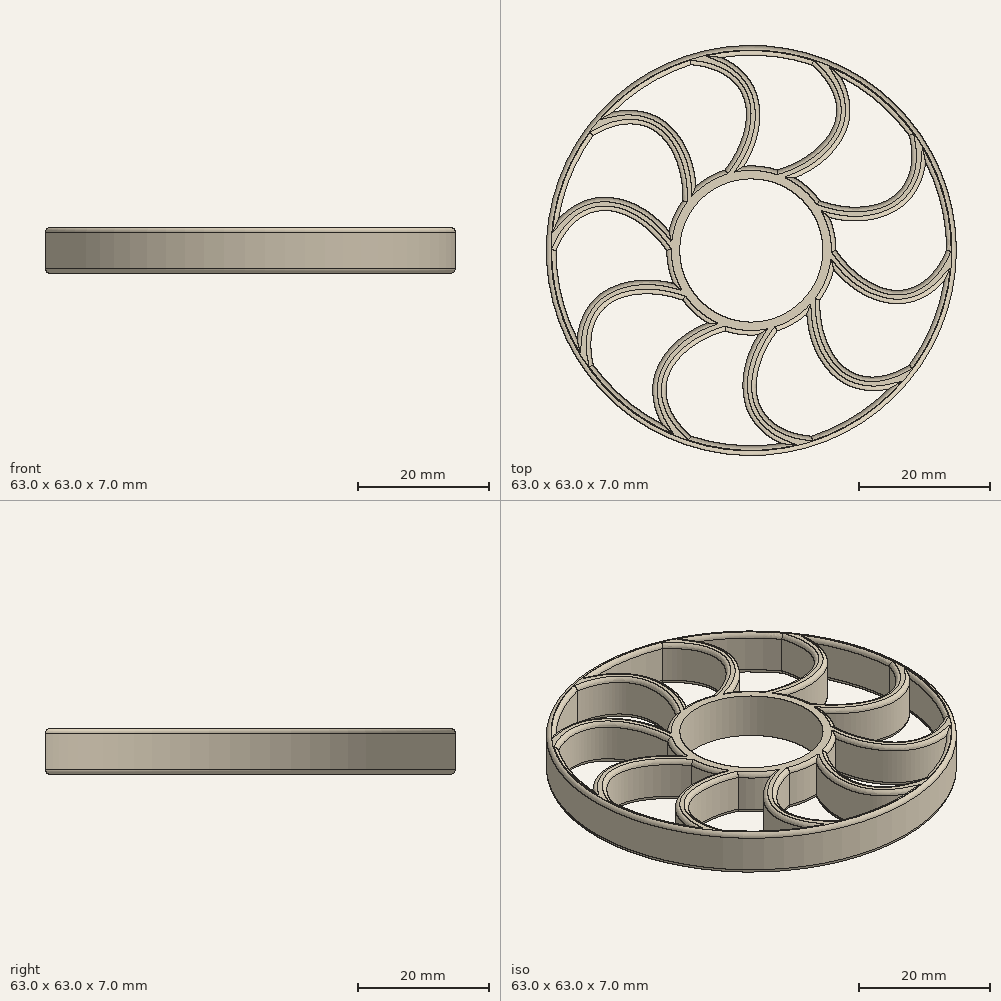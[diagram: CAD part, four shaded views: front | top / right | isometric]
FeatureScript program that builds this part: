
annotation { "Feature Type Name" : "Feature", "Feature Type Description" : "" }
export const myFeature = defineFeature(function(context is Context, id is Id, definition is map)
    precondition{}
    {
        {
            var Q0;
            Q0=qCreatedBy(makeId("Top.planeOp"),FACE);
            var sketch = newSketch(context, id + "F0", { "sketchPlane" : qUnion([Q0])});
            skCircle(sketch, "E0", {"center": v(0, 0) * mm, "radius": 11 * mm});
            skArc(sketch, "E1", {"start": v(30, 0) * mm, "mid": v(-29.92, 2.25) * mm, "end": v(29.66, -4.48) * mm});
            skArc(sketch, "E2", {"start": v(13, 0) * mm, "mid": v(-12.92, 1.44) * mm, "end": v(12.68, -2.86) * mm});
            skCircle(sketch, "E3", {"center": v(0, 0) * mm, "radius": 31.5 * mm});
            skFitSpline(sketch, "E4", {"points": [v(13, 0) * mm, v(22.2, -6.13) * mm, v(30, 0) * mm], "startDerivative": vector(13.65, -20) * mm, "endDerivative": vector(11.01, 26.01) * mm});
            skFitSpline(sketch, "E5.0", {"points": [v(11.35, -1.13) * mm, v(11.98, -2.06) * mm, v(13.41, -3.8) * mm, v(15.92, -5.95) * mm, v(18.26, -7.25) * mm, v(20.24, -7.9) * mm, v(21.78, -8.16) * mm, v(23.35, -8.14) * mm, v(24.88, -7.85) * mm, v(26.34, -7.27) * mm, v(28.16, -6.15) * mm, v(30.12, -4.15) * mm, v(31.33, -2) * mm, v(31.84, -0.78) * mm]});
            skSolve(sketch);
        }
        {
            var Q0;
            Q0=makeQuery(id+"F0.imprint","IMPRINT",FACE,{"disambiguationData":[TD([[makeQuery(id+"F0.imprint","IMPRINT",EDGE,{"derivedFrom":sQuery(id+"F0.wireOp",EDGE,"E0")}),-1.0]])]});
            var Q1;
            Q1=makeQuery(id+"F0.imprint","IMPRINT",FACE,{"disambiguationData":[TD([[makeQuery(id+"F0.imprint","IMPRINT",EDGE,{"derivedFrom":sQuery(id+"F0.wireOp",EDGE,"E3")}),1.0]])]});
            extrude(context, id + "F1", {"entities" : qUnion([Q0, Q1]), "depth" : 3.5 * mm, "offsetDistance" : 25 * mm});
        }
        {
            var Q0;
            {var subQ0=sQuery(id+"F0.wireOp",EDGE,"E4");Q0=makeQuery(id+"F0.imprint","IMPRINT",FACE,{"disambiguationData":[TD([[makeQuery(id+"F0.imprint","IMPRINT",EDGE,{"derivedFrom":subQ0}),-1.0]])]});}
            extrude(context, id + "F2", {"entities" : qUnion([Q0]), "depth" : 3.5 * mm, "offsetDistance" : 25 * mm});
        }
        {
            var Q0;
            Q0=makeQuery(id+"F1.opExtrude","CAP_EDGE",EDGE,{"disambiguationData":[OSD([sQuery(id+"F0.wireOp",EDGE,"E2")])],"isStart":false});
            var Q1;
            Q1=makeQuery(id+"F1.opExtrude","CAP_EDGE",EDGE,{"disambiguationData":[OSD([sQuery(id+"F0.wireOp",EDGE,"E5.0")])],"isStart":false});
            var Q2;
            Q2=makeQuery(id+"F1.opExtrude","CAP_EDGE",EDGE,{"disambiguationData":[OSD([sQuery(id+"F0.wireOp",EDGE,"E4")])],"isStart":false});
            var Q3;
            Q3=makeQuery(id+"F1.opExtrude","CAP_EDGE",EDGE,{"disambiguationData":[OSD([sQuery(id+"F0.wireOp",EDGE,"E3")])],"isStart":false});
            var Q4;
            Q4=makeQuery(id+"F1.opExtrude","CAP_EDGE",EDGE,{"disambiguationData":[OSD([sQuery(id+"F0.wireOp",EDGE,"E1")])],"isStart":false});
            fillet(context, id + "F3", {"entities" : qUnion([Q0, Q1, Q2, Q3, Q4]), "radius" : .7 * mm, "tangentPropagation" : true, "allowEdgeOverflow" : false});
        }
        {
            var Q0;
            Q0=makeQuery(id+"F2.opExtrude","SWEPT_BODY",BODY,{"disambiguationData":[OSD([sQuery(id+"F0.wireOp",EDGE,"E0"),sQuery(id+"F0.wireOp",EDGE,"E1"),sQuery(id+"F0.wireOp",EDGE,"E2"),sQuery(id+"F0.wireOp",EDGE,"E3"),sQuery(id+"F0.wireOp",EDGE,"E4"),sQuery(id+"F0.wireOp",EDGE,"E5.0")])]});
            deleteBodies(context, id + "F4", {"entities" : qUnion([Q0])});
        }
        {
            var Q0;
            Q0=makeQuery(id+"F1.opExtrude","SWEPT_BODY",BODY,{"disambiguationData":[OSD([sQuery(id+"F0.wireOp",EDGE,"E0"),sQuery(id+"F0.wireOp",EDGE,"E1"),sQuery(id+"F0.wireOp",EDGE,"E2"),sQuery(id+"F0.wireOp",EDGE,"E3"),sQuery(id+"F0.wireOp",EDGE,"E4"),sQuery(id+"F0.wireOp",EDGE,"E5.0")])]});
            var Q1;
            Q1=makeQuery(id+"F1.opExtrude","CAP_EDGE",EDGE,{"disambiguationData":[OSD([sQuery(id+"F0.wireOp",EDGE,"E0")])],"isStart":false});
            circularPattern(context, id + "F5", {"operationType" : NewBodyOperationType.ADD, "entities" : qUnion([Q0]), "axis" : qUnion([Q1]), "angle" : 360 * degree, "instanceCount" : 10, "oppositeDirection" : true, "equalSpace" : true});
        }
        {
            var Q0;
            Q0=makeQuery(id+"F1.opExtrude","SWEPT_BODY",BODY,{"disambiguationData":[OSD([sQuery(id+"F0.wireOp",EDGE,"E0"),sQuery(id+"F0.wireOp",EDGE,"E1"),sQuery(id+"F0.wireOp",EDGE,"E2"),sQuery(id+"F0.wireOp",EDGE,"E3"),sQuery(id+"F0.wireOp",EDGE,"E4"),sQuery(id+"F0.wireOp",EDGE,"E5.0")])]});
            var Q1;
            Q1=qCreatedBy(makeId("Top.planeOp"),FACE);
            mirror(context, id + "F6", {"operationType" : NewBodyOperationType.ADD, "entities" : qUnion([Q0]), "mirrorPlane" : qUnion([Q1])});
        }
    });
